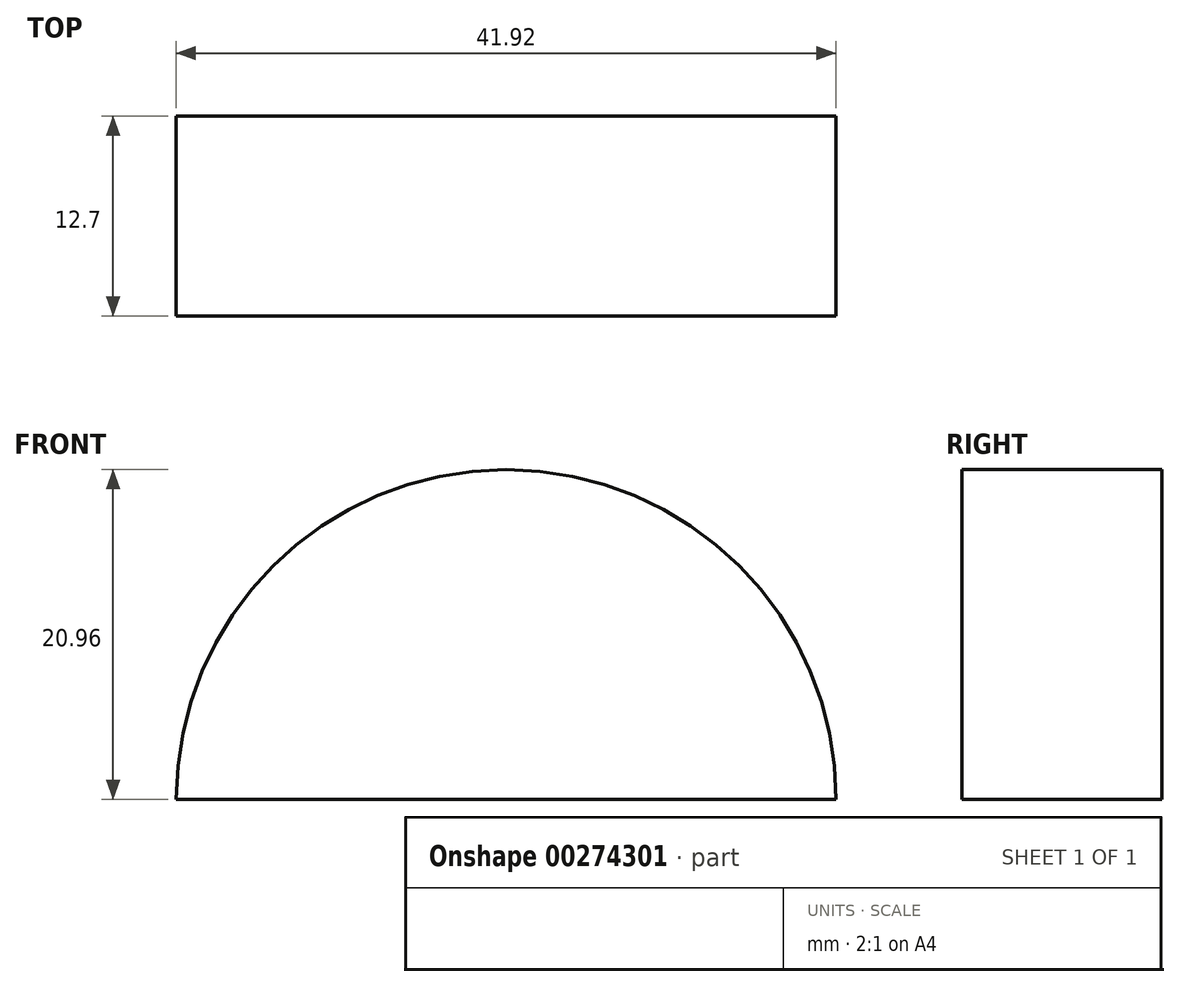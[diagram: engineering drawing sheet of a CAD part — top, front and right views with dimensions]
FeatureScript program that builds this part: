
annotation { "Feature Type Name" : "Feature", "Feature Type Description" : "" }
export const myFeature = defineFeature(function(context is Context, id is Id, definition is map)
    precondition{}
    {
        {
            var Q0;
            Q0=qCreatedBy(makeId("Front.planeOp"),FACE);
            var sketch = newSketch(context, id + "F0", { "sketchPlane" : qUnion([Q0])});
            skLineSegment(sketch, "E0", {"start": v(0, 0) * mm, "end": v(20.96, 0) * mm});
            skLineSegment(sketch, "E1", {"start": v(0, 0) * mm, "end": v(-20.96, 0) * mm});
            skLineSegment(sketch, "E2", {"start": v(0, 0) * mm, "end": v(0, 20.96) * mm});
            skArc(sketch, "E3", {"start": v(20.96, 0) * mm, "mid": v(0, 20.96) * mm, "end": v(-20.96, 0) * mm});
            skSolve(sketch);
        }
        {
            var Q0;
            {var subQ0=sQuery(id+"F0.wireOp",EDGE,"E0");Q0=makeQuery(id+"F0.imprint","IMPRINT",FACE,{"disambiguationData":[TD([[makeQuery(id+"F0.imprint","IMPRINT",EDGE,{"derivedFrom":subQ0}),1.0]])]});}
            var Q1;
            {var subQ0=sQuery(id+"F0.wireOp",EDGE,"E1");Q1=makeQuery(id+"F0.imprint","IMPRINT",FACE,{"disambiguationData":[TD([[makeQuery(id+"F0.imprint","IMPRINT",EDGE,{"derivedFrom":subQ0}),-1.0]])]});}
            extrude(context, id + "F1", {"entities" : qUnion([Q0, Q1]), "depth" : 12.7 * mm});
        }
    });
